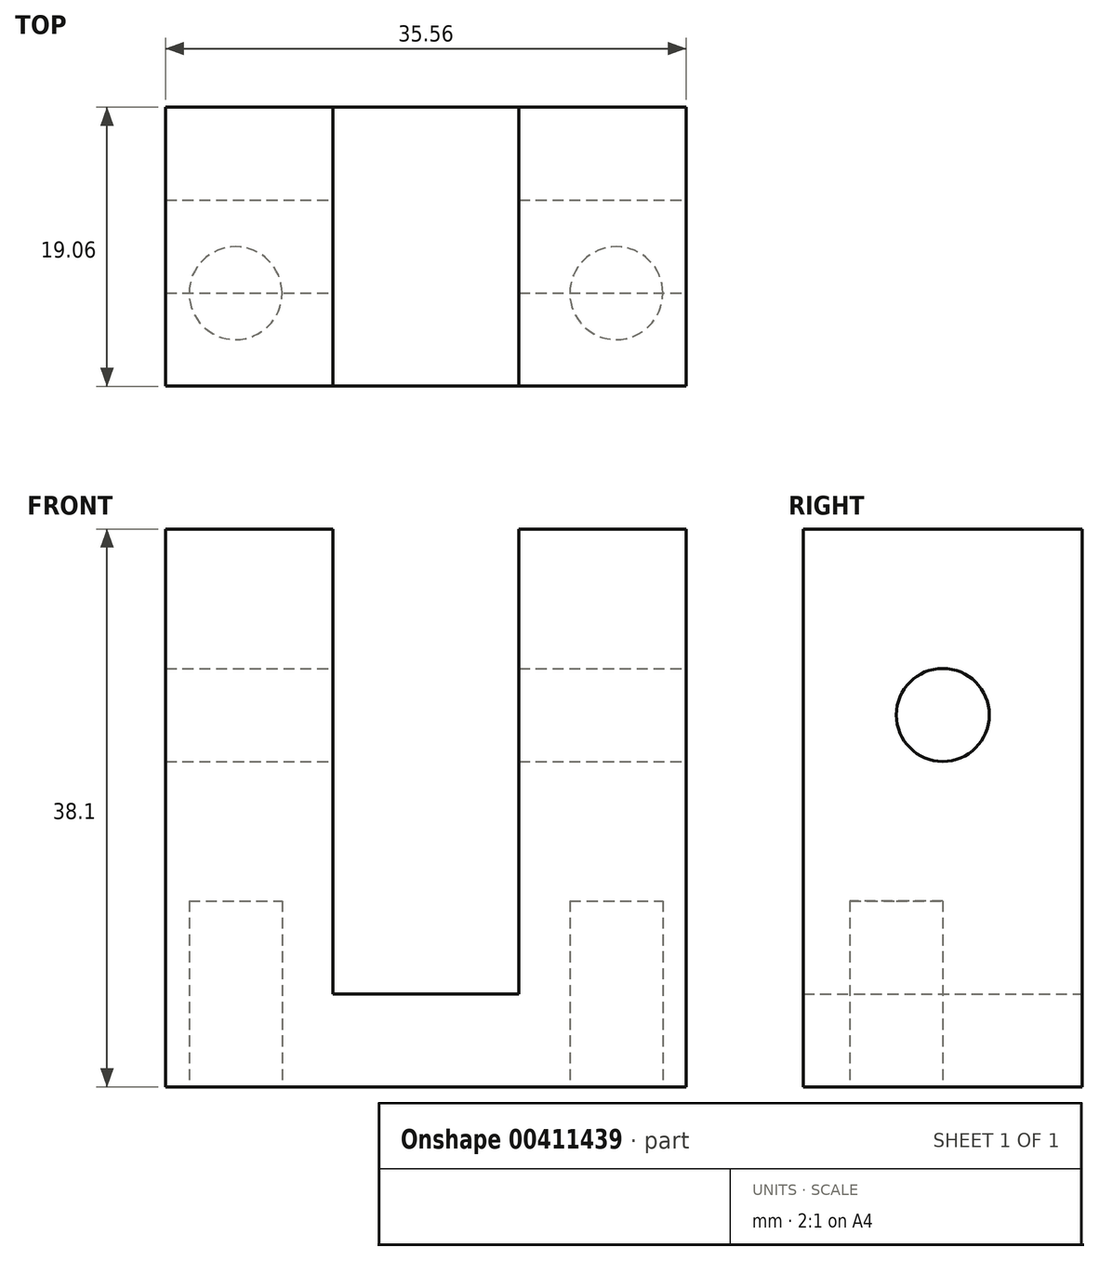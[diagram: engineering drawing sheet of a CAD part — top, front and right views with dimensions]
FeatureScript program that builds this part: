
annotation { "Feature Type Name" : "Feature", "Feature Type Description" : "" }
export const myFeature = defineFeature(function(context is Context, id is Id, definition is map)
    precondition{}
    {
        {
            var Q0;
            Q0=qCreatedBy(makeId("Front.planeOp"),FACE);
            var sketch = newSketch(context, id + "F0", { "sketchPlane" : qUnion([Q0])});
            skLineSegment(sketch, "E0", {"start": v(-17.78, 12.7) * mm, "end": v(-17.78, -25.4) * mm});
            skLineSegment(sketch, "E1", {"start": v(-17.78, -25.4) * mm, "end": v(17.78, -25.4) * mm});
            skLineSegment(sketch, "E2", {"start": v(17.78, -25.4) * mm, "end": v(17.78, 12.7) * mm});
            skLineSegment(sketch, "E3", {"start": v(17.78, 12.7) * mm, "end": v(6.35, 12.7) * mm});
            skLineSegment(sketch, "E4", {"start": v(6.35, 12.7) * mm, "end": v(6.35, -19.05) * mm});
            skLineSegment(sketch, "E5", {"start": v(6.35, -19.05) * mm, "end": v(-6.35, -19.05) * mm});
            skLineSegment(sketch, "E6", {"start": v(-6.35, -19.05) * mm, "end": v(-6.35, 12.7) * mm});
            skLineSegment(sketch, "E7", {"start": v(-6.35, 12.7) * mm, "end": v(-17.78, 12.7) * mm});
            skSolve(sketch);
        }
        {
            var Q0;
            Q0=qSketchRegion(id+"F0",true);
            extrude(context, id + "F1", {"entities" : qUnion([Q0]), "endBound" : BoundingType.SYMMETRIC, "depth" : 19.05 * mm});
        }
        {
            var Q0;
            Q0=makeQuery(id+"F1.opExtrude","SWEPT_FACE",FACE,{"disambiguationData":[OSD([sQuery(id+"F0.wireOp",EDGE,"E2")])]});
            var sketch = newSketch(context, id + "F2", { "sketchPlane" : qUnion([Q0])});
            skCircle(sketch, "E8", {"center": v(0, 0) * mm, "radius": 3.17 * mm});
            skSolve(sketch);
        }
        {
            var Q0;
            Q0=qSketchRegion(id+"F2",true);
            var Q1;
            Q1=makeQuery(id+"F1.opExtrude","SWEPT_FACE",FACE,{"disambiguationData":[OSD([sQuery(id+"F0.wireOp",EDGE,"E0")])]});
            extrude(context, id + "F3", {"entities" : qUnion([Q0]), "operationType" : NewBodyOperationType.REMOVE, "endBound" : BoundingType.UP_TO_SURFACE, "oppositeDirection" : true, "endBoundEntityFace" : qUnion([Q1]), "depth" : 25.4 * mm});
        }
        {
            var Q0;
            Q0=makeQuery(id+"F1.opExtrude","SWEPT_FACE",FACE,{"disambiguationData":[OSD([sQuery(id+"F0.wireOp",EDGE,"E1")])]});
            var sketch = newSketch(context, id + "F4", { "sketchPlane" : qUnion([Q0])});
            skCircle(sketch, "E9", {"center": v(-13, 3.17) * mm, "radius": 3.18 * mm});
            skCircle(sketch, "E10", {"center": v(13, 3.18) * mm, "radius": 3.18 * mm});
            skSolve(sketch);
        }
        {
            var Q0;
            Q0=qSketchRegion(id+"F4",true);
            extrude(context, id + "F5", {"entities" : qUnion([Q0]), "operationType" : NewBodyOperationType.REMOVE, "oppositeDirection" : true, "depth" : 12.7 * mm});
        }
    });
